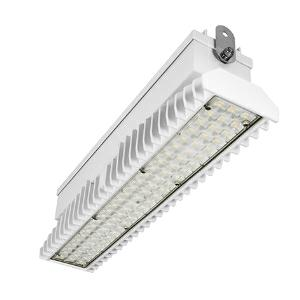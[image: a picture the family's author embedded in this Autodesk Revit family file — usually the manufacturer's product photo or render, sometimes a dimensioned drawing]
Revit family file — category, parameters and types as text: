
# Revit family: 3f_filippi_-_3f_lem_ho_concentrato_3f_filippi_-_58977_a0811_-_3f_lem_1_ho_led_70_dali_cr_conc___vt_2a81
name_source: partatom
category: Lighting Fixtures
units: mm (PartAtom-declared; Revit-internal decimal feet)

## family parameters
Cut with Voids When Loaded = No
Host = Face
Light Source = No
Part Type = Normal
Room Calculation Point = No
Round Connector Dimension = Use Diameter
Shared = No

## types (1)
- 3F Filippi - 3F LEM HO Concentrato (1 x LED, 10083 lm, 71 W, 4000 K)
    Apparent Load = 71 VA
    Approval mark = CE
    CIE Flux Codes = 83 96 99 100 100
    Color Rendering = 80
    Color Temperature = 4000 K
    Control Gear = Electronic transformer
    Default Elevation = 1800 mm
    Description = Industrial luminaire with high light output and high luminous efficiency designed with the most innovative technologies for environments with temperature up to 55°C.

ILLUMINOTECHNICAL
Luminous efficiency 100% (DLOR 99%, ULOR 1%).
Initial luminous flux of the luminaire 10083 lm.
Direct symmetric narrow distribution: the illuminated area has a elliptical shape.
Installation Interdistance Transv.D = 0.52 x hu - Long.D = 1.16 x hu.
Tabular UGR (CIE 117 - 4H-8H; S=0.25H; 70/50/20): RUG 21.2 - 25.
Beam angle: 31° - 73°.
Luminous efficacy 142 lm/W.
Lifetime (L93/B10): 30000 h. (tq+25°C)
Lifetime (L90/B10): 50000 h. (tq+25°C)
Lifetime (L85/B10): 80000 h. (tq+25°C)
Lifetime (L80/B10): 100000 h. (tq+25°C)
Lifetime (L85/B10): 50000 h. (tq+55°C)
Sudden decreased luminous flux after 50000 hours: 0% (C0).
Photobiological safety in compliance with IEC/TR 62778: RG0 risk exempt, (IEC 62471).
In compliance with IEC/EN 62722-2-1 - IEC/EN 62717 standards.

SOURCE
Mid-Power linear LED module 70W/840.
Energy efficiency class (UE 2019/2020 - UE 2019/2015): C.
CIE 13.3 Colour rendering index: CRI >80 (R9 <50%).
IES TM-30 Fidelity Index: Rf = 84 Rg = 95.
CCT nominal colour temperature 4000 K.
Colour initial tolerance (MacAdam): SDCM 3.

MECHANICAL
Passive modular heatsinks in die-casted aluminium, painted in white colour.
To optimize the thermal management of the LED module, the heatsinks are oversized and provided with self-cleaning of cooling fins.
Wiring body in aluminium and galvanised steel anchored solidly to the sinks and thermally separated.
3F Lens lenses with high luminous efficiency, transparent methacrylate (PMMA), fixed to the LED modules.
Fixing brackets in stainless steel.
Luminaire with limited surface temperature. - D - (EN 60598-2-24)
Dimensions: 542x115 mm, height 154 mm. Weight 6.717 kg.
IP65 protection degree.
Mechanical strength to impacts IK06 (1 joule).
Glow-wire test resistance 650°C.

ELECTRICAL
Halogen Free DALI-2 DATI (Parts 251, 252, 253), PUSH-DIM, electronic wiring 230V-50/60Hz, power factor 0.97 at full load, THD <25%, constant output current, class I, 1 driver, 1 DALI addresse.
Power of the luminaire 71 W.
ENEC - CE.
SAFE FLICKER: PstLM=<1 and SVM=<0.4 (IEC TR 61547-1 and IEC TR 63158), to ensure a more comfortable and safe light.
Luminaire compliant with EN 60598-2-22 for power supply from a centralised emergency system CPSS (Central Power Supply System), not incorporated in the luminaire - high risk areas excluded. The default power and flux are 100% in AC and 15% in DC.
Ambient temperature from -30°C to +55°C.
Temperature class T6 max 85°C.
Quick connection via M25 5P connector with 9-13 mm tightening range.
Power unit positioned on a separate compartment by the LED module to ensure optimum temperatures of cabling components, to be inspectable and maintainable.
Relative humidity UR: <85%.

INSTALLATION
Ceiling / Suspended / Wall.
All accessories dedicated to this product are available on the Catalog and on our website www.3F-Filippi.com.

ACCESSORIES
A0811 - VT transparent glass, tempered, not flammable, with sealing gasket.
One required for each light module. The pack contains 10 pieces.

APPLICATIONS
In commercial environments, exhibition and industrial areas, stores, open areas or with shelves.
Environments in which it is necessary a total protection against falling fragments (eg environments with foodstuffs or machines with moving parts or with extreme temperature changes), use luminaires with polycarbonate lenses.

LIGHT MANAGEMENT
Recommended minimum setting: 10%.
The luminaire, equipped with (DALI-2 DATI) driver, can be controlled manually with 3F Easy Dim technology or automatically/manually with wired or wireless DALI/D2D control systems.
The D2D driver guarantees interoperability with other devices with the same certification by making the following information available:
Device Data (Part 251), Energy Report (Part 252), Diagnosis & Maintenance (Part 253).
In electrical systems without a regulation system (manual or automatic) and DALI bus, a suitable jumper must be made on the DA-DA terminals of the appliance.

WARNING
Fixture not suitable for cold stores with an ambient temperature <0°C and/or relative humidity >85%.
Luminaire designed for disposal/recycling at end-of-life.
Replaceable (LED only) light source by a professional. Replaceable control gear by a professional.
    Height = 154 mm
    Lamp = 1 x LED
    Lamp Light Flux = 10083 lm
    Lamp Power = 71 W
    Lamp count = 1
    Length = 542 mm
    Lifetime = 50000 h
    Luminous efficacy = 142 lm/W
    Manufacturer = 3F Filippi
    ModVariant = No
    Model = 3F Filippi - 58977+A0811 - 3F LEM 1 HO LED 70 DALI CR CONC + VT
    Mounting Place = Ceiling
    Mounting Type = Pendant
    Number of Poles = 1
    OnlyDefault = Yes
    Power Factor = 1
    Product Name = 3F Filippi - 3F LEM HO Concentrato
    Product group = pendant luminaire
    ProductGroupID = 9
    Protection Class = Protection class I
    Protection Degree = IP 65
    RLX_Detail_Level = 1
    RLX_Emergency_Light_Flux = 0 lm
    RLX_Emergency_Type = 0
    RLX_Emergency_Type_DB = No
    RlxData = <blob elided: 96865 chars, md5=39caaff5>
    Socket = socket
    Standby Power = 0 W
    System Light Flux = 10083 lm
    System Power = 71 W
    Type Comments = Product without accessories
    Type Image = 3f_filippi_-_lem_1__a0811.jpg
    URL = http://relux.com
    VarID = ---
    Voltage = 0 V
    Weight = 0.00 kg
    Width = 115 mm

## geometry (parser evidence)
native form markers: Blend x4, Sweep x11
no freeform markers — native parametric forms only
